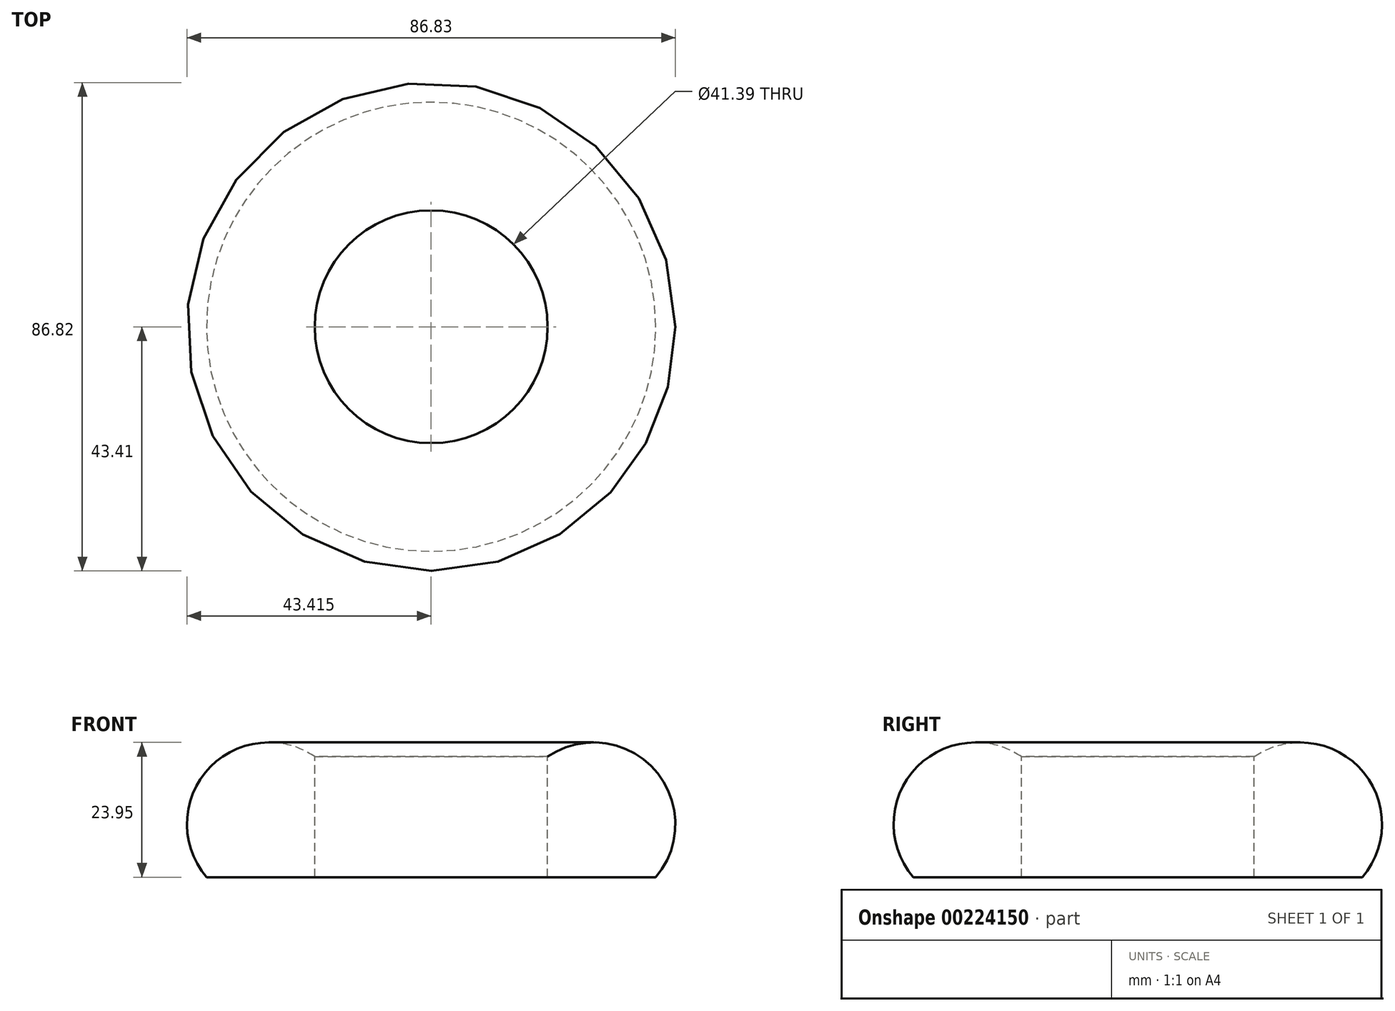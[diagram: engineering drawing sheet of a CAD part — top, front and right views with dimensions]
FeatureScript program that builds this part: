
annotation { "Feature Type Name" : "Feature", "Feature Type Description" : "" }
export const myFeature = defineFeature(function(context is Context, id is Id, definition is map)
    precondition{}
    {
        {
            var Q0;
            Q0=qCreatedBy(makeId("Front.planeOp"),FACE);
            var sketch = newSketch(context, id + "F0", { "sketchPlane" : qUnion([Q0])});
            skLineSegment(sketch, "E0", {"start": v(0, 21.42) * mm, "end": v(0, 0) * mm});
            skLineSegment(sketch, "E1", {"start": v(19.24, 0) * mm, "end": v(0, 0) * mm});
            skArc(sketch, "E2", {"start": v(19.24, 0) * mm, "mid": v(19, 19.13) * mm, "end": v(0, 21.42) * mm});
            skSolve(sketch);
        }
        {
            var Q0;
            Q0=qCreatedBy(makeId("Front.planeOp"),FACE);
            var sketch = newSketch(context, id + "F1", { "sketchPlane" : qUnion([Q0])});
            skLineSegment(sketch, "E3", {"start": v(-20.7, 19.1) * mm, "end": v(-20.7, -12.97) * mm});
            skSolve(sketch);
        }
        {
            var Q0;
            Q0=makeQuery(id+"F0.imprint","IMPRINT",FACE,{"disambiguationData":[TD([[makeQuery(id+"F0.imprint","IMPRINT",EDGE,{"derivedFrom":sQuery(id+"F0.wireOp",EDGE,"E0")}),1.0]])]});
            var Q1;
            Q1=sQuery(id+"F1.wireOp",EDGE,"E3");
            revolve(context, id + "F2", {"entities" : qUnion([Q0]), "axis" : qUnion([Q1]), "revolveType" : RevolveType.FULL});
        }
    });
